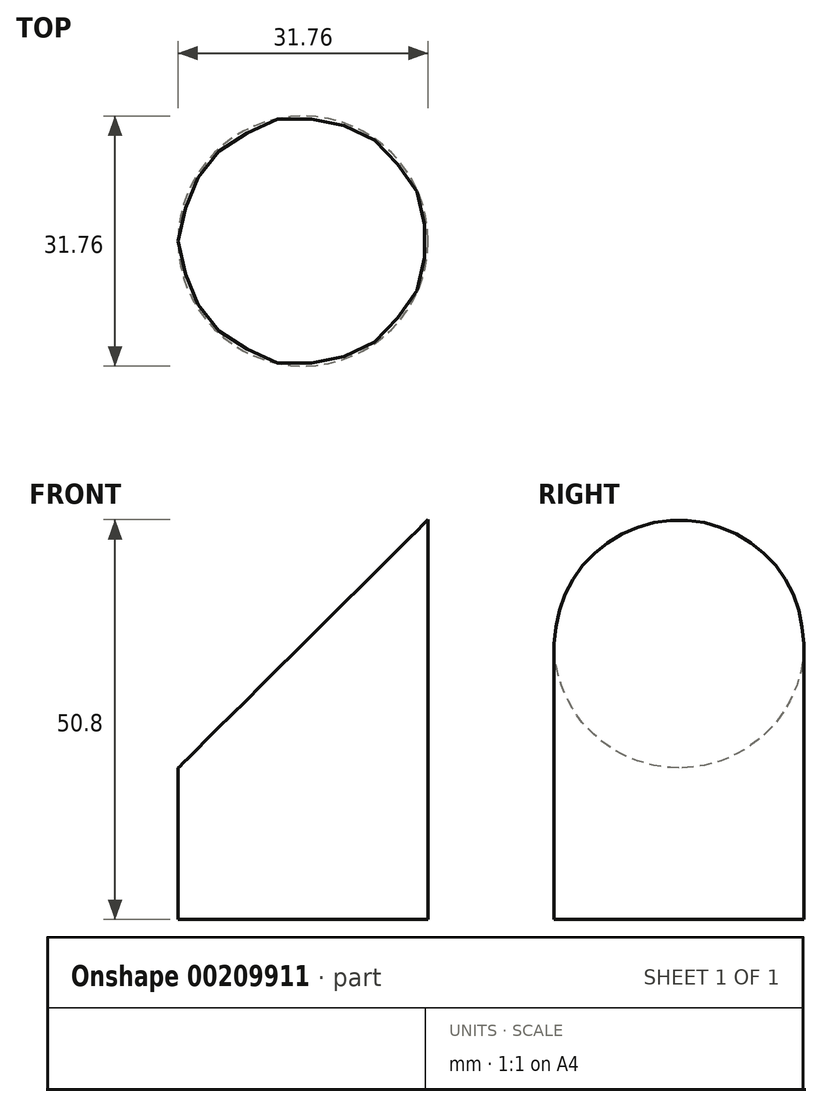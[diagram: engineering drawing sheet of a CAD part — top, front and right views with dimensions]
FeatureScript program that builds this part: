
annotation { "Feature Type Name" : "Feature", "Feature Type Description" : "" }
export const myFeature = defineFeature(function(context is Context, id is Id, definition is map)
    precondition{}
    {
        {
            var Q0;
            Q0=qCreatedBy(makeId("Top.planeOp"),FACE);
            var sketch = newSketch(context, id + "F0", { "sketchPlane" : qUnion([Q0])});
            skCircle(sketch, "E0", {"center": v(0, 0) * mm, "radius": 15.88 * mm});
            skSolve(sketch);
        }
        {
            var Q0;
            Q0=makeQuery(id+"F0.imprint","IMPRINT",FACE,{"disambiguationData":[TD([[makeQuery(id+"F0.imprint","IMPRINT",EDGE,{"derivedFrom":sQuery(id+"F0.wireOp",EDGE,"E0")}),1.0]])]});
            extrude(context, id + "F1", {"entities" : qUnion([Q0]), "depth" : 50.8 * mm});
        }
        {
            var Q0;
            Q0=qCreatedBy(makeId("Front.planeOp"),FACE);
            var sketch = newSketch(context, id + "F2", { "sketchPlane" : qUnion([Q0])});
            skLineSegment(sketch, "E1.0", {"start": v(-15.88, 50.8) * mm, "end": v(15.88, 50.8) * mm});
            skLineSegment(sketch, "E2", {"start": v(15.88, 50.8) * mm, "end": v(-16.06, 19.05) * mm});
            skLineSegment(sketch, "E3", {"start": v(-16.06, 19.05) * mm, "end": v(-15.88, 50.8) * mm});
            skSolve(sketch);
        }
        {
            var Q0;
            Q0 = qSketchRegion(id + "F2", true);
            extrude(context, id + "F3", {"entities" : qUnion([Q0]), "operationType" : NewBodyOperationType.REMOVE, "endBound" : BoundingType.SYMMETRIC, "oppositeDirection" : true, "depth" : 50.8 * mm});
        }
    });
